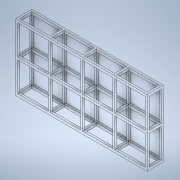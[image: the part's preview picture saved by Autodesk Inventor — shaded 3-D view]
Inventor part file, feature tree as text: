
AUTODESK INVENTOR PART (.ipt)
format: ipt  version: 2022 (Build 260153000, 153)  size: 360,960 bytes
history: native  units: in
note: dims shown in document units (in); Inventor stores cm internally (conversion verified against a paired STEP export)
features: extrude x4, sketch x4, other x1, pattern_linear x1
ambient origin geometry x8: Origin, YZ Plane, XZ Plane, XY Plane, X Axis, Y Axis, Z Axis, Center Point
bodies: Solid1 (feature_tree)
feature tree (10):
  other  "CustomAquariumsStand"
  extrude  "Extrusion1"  Depth=48.0in
  extrude  "Extrusion2"  Depth=97.5in
  extrude  "Extrusion3"  Depth=94.5in
  extrude  "Extrusion4"  Depth=1.5in TaperAngle=0.0deg
  pattern_linear  "Rectangular Pattern1"  Spacing1=12.0in  [1 undecoded]
  sketch  "Sketch1"  dims[d0=96.0in d1=48.0in]
  sketch  "Sketch2"  dims[d2=0.75in d3=0.0in d4=97.5in]
  sketch  "Sketch4"  dims[d5=49.5in d6=94.5in]
  sketch  "Sketch5"  dims[d7=45.5in d8=1.5in d9=0.0in d18=12.0in d19=0.0in d28=1.5in d29=0.0in d30=0.7874in d32=10.5in d33=1.9685in d35=24.0in d36=1.1811in d38=23.75in d41=1.5748in d43=24.0in d44=0.7874in d46=23.75in]
note: 1 required parameter value undecoded (feature->parameter linkage not recoverable at this tier; creation-order binding heuristic only, values carry confidence <= 0.55)
